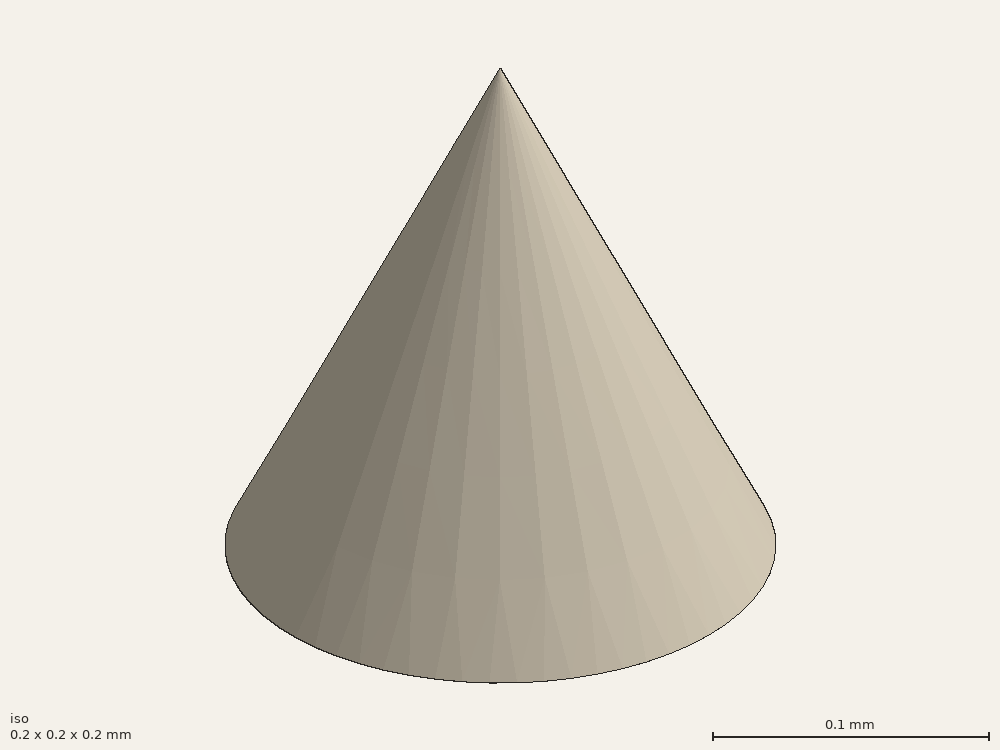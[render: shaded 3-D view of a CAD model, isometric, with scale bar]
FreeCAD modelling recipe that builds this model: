
FCSTD DOCUMENT  (FreeCAD 0.18R)
Label: CICLOIDE
License: All rights reserved
LicenseURL: http://en.wikipedia.org/wiki/All_rights_reserved
objects: App::DocumentObjectGroupPython×3, Part::Circle×2, Part::Vertex×1, Part::Loft×1, Part::Part2DObjectPython×1
note: 5 computed .brp shape members not serialized (recipe doc carries the construction recipe); baked Part::Feature solids carry a one-line shape summary decoded from their .brp

FEATURE [Part::Vertex] Vertex
  AttacherType = Attacher::AttachEngine3D
  X = 0
  Y = 0
  Z = 0
FEATURE [Part::Circle] Circle
  Angle0 = 0
  Angle1 = 360
  AttacherType = Attacher::AttachEngine3D
  Placement = pos=(0,0,-0.2) rot=(0,0,1;0rad)
  Radius = 0.1
FEATURE [Part::Loft] Loft
  Closed = false
  MaxDegree = 5
  Placement = pos=(0.933899,1.30902,0) rot=(0,0,1;0rad)
  Ruled = false
  Sections = -> [Vertex,Circle]
  Solid = true
FEATURE [App::DocumentObjectGroupPython] My_Placer  # scripted group (container) (typed FeaturePython)
  Placement = pos=(0.933899,1.30902,0) rot=(0,0,1;0rad)
  RotAxis = (0,0,1)
  RotCenter = (0,0,0)
  arc = 0
  arc0 = 0
  arc1 = 90
  target = -> Loft
  time = 0.3
  x = x1-y0
  x0 = -0.309017
  x1 = 1.88496
  y = 1-x0
  y0 = 0.951057
  y1 = 0
  z = 0
  z0 = 0
  z1 = 0
  expr: x1 = time * pi * 2
  expr: y0 = sin(time * 360)
  expr: x0 = cos(time * 360)
FEATURE [Part::Part2DObjectPython] BSpline  # Draft 2D object (typed FeaturePython)
  Closed = false
  MakeFace = false
  Parameterization = 1
  Points = (14) [(0,0,0),(0.0140437,0.0951729,0),(0.226146,0.574221,0),(0.509938,0.937209,0),(1.10579,1.42578,0),(1.81302,1.77051,0),(2.51842,1.95106,0),+7 more]
FEATURE [Part::Circle] Circle001
  Angle0 = 0
  Angle1 = 360
  AttacherType = Attacher::AttachEngine3D
  Placement = pos=(1.88496,1,0) rot=(0,0,1;0rad)
  Radius = 1
FEATURE [App::DocumentObjectGroupPython] My_Placer001  # scripted group (container) (typed FeaturePython)
  Placement = pos=(1.88496,1,0) rot=(0,0,1;0rad)
  RotAxis = (0,0,1)
  RotCenter = (0,0,0)
  arc = 0
  arc0 = 0
  arc1 = 90
  target = -> Circle001
  time = 0.3
  x = x0
  x0 = 1.88496
  x1 = 200
  y = 1
  y0 = 0
  y1 = 0
  z = 0
  z0 = 0
  z1 = 0
  expr: x0 = 2 * time * pi
FEATURE [App::DocumentObjectGroupPython] My_Manager  # scripted group (container) (typed FeaturePython)
  Group = -> [My_Placer,My_Placer001]
  intervall = 100
  sleeptime = 0.02
  start = 0
  step = 30
  text = NO
